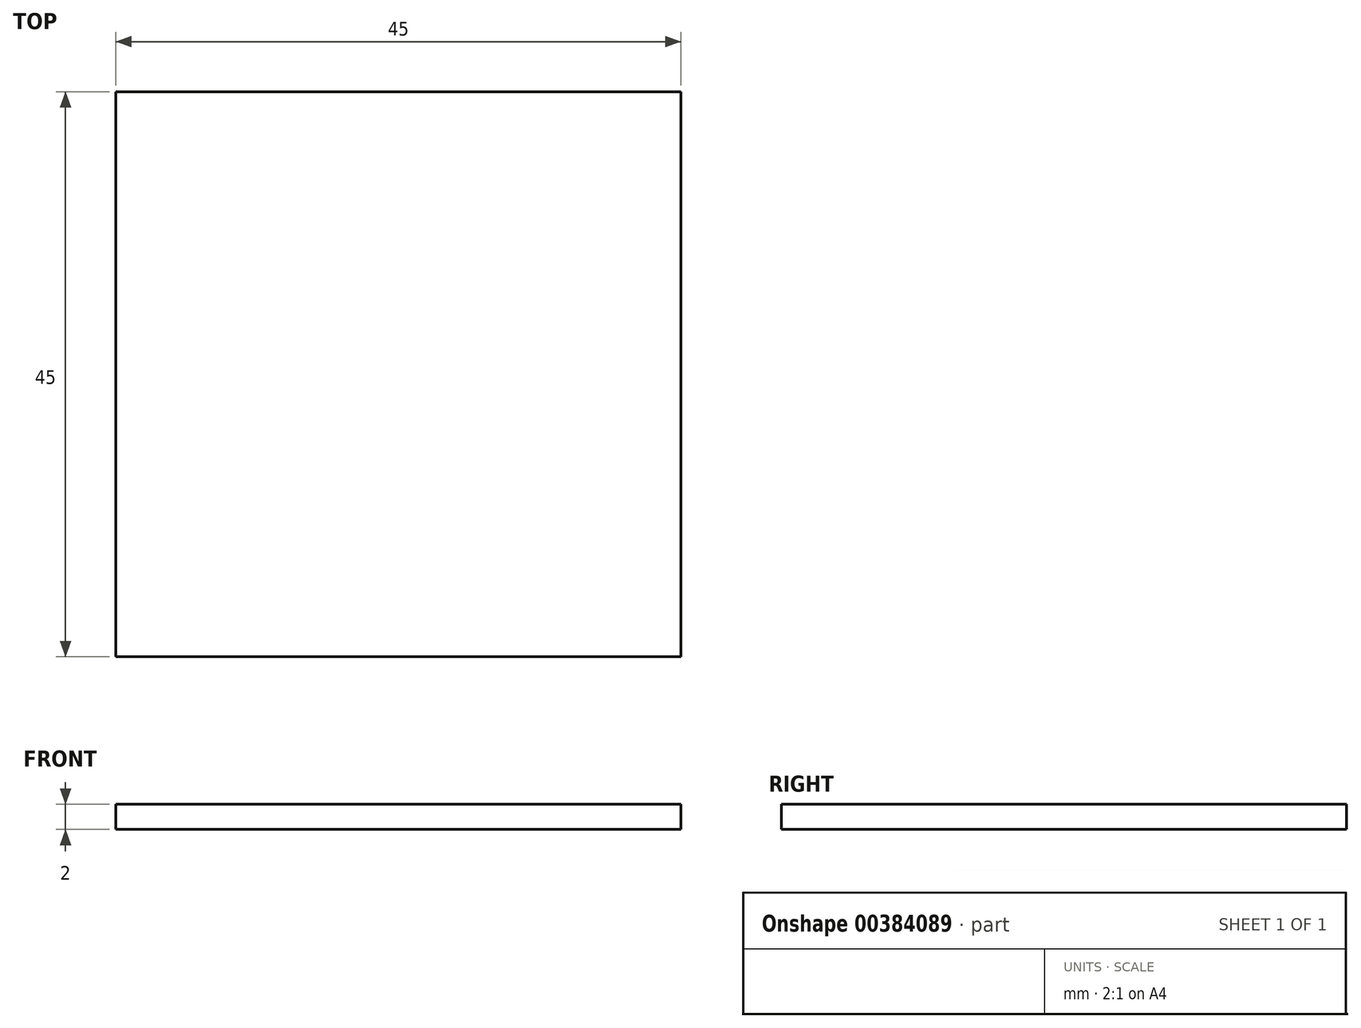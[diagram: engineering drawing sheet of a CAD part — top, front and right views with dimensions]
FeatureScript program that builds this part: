
annotation { "Feature Type Name" : "Feature", "Feature Type Description" : "" }
export const myFeature = defineFeature(function(context is Context, id is Id, definition is map)
    precondition{}
    {
        {
            var Q0;
            Q0=qCreatedBy(makeId("Top.planeOp"),FACE);
            var sketch = newSketch(context, id + "F0", { "sketchPlane" : qUnion([Q0])});
            skLineSegment(sketch, "E0.bottom", {"start": v(-14, 28.89) * mm, "end": v(31, 28.89) * mm});
            skLineSegment(sketch, "E0.top", {"start": v(-14, -16.11) * mm, "end": v(31, -16.11) * mm});
            skLineSegment(sketch, "E0.left", {"start": v(-14, 28.89) * mm, "end": v(-14, -16.11) * mm});
            skLineSegment(sketch, "E0.right", {"start": v(31, 28.89) * mm, "end": v(31, -16.11) * mm});
            skSolve(sketch);
        }
        {
            var Q0;
            Q0=makeQuery(id+"F0.imprint","IMPRINT",FACE,{"disambiguationData":[TD([[makeQuery(id+"F0.imprint","IMPRINT",EDGE,{"derivedFrom":sQuery(id+"F0.wireOp",EDGE,"E0.bottom")}),-1.0]])]});
            extrude(context, id + "F1", {"entities" : qUnion([Q0]), "depth" : 2 * mm});
        }
    });
